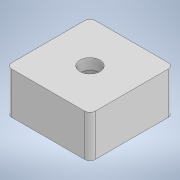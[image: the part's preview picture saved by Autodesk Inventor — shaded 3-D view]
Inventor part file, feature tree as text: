
AUTODESK INVENTOR PART (.ipt)
format: ipt  version: 2021 (Build 250183000, 183)  size: 146,432 bytes
history: native  units: mm
features: sketch x5, extrude x3, other x2, hole x2, fillet x1, projected_geometry x1
ambient origin geometry x8: Origin, YZ Plane, XZ Plane, XY Plane, X Axis, Y Axis, Z Axis, Center Point
bodies: Body1 (feature_tree)
feature tree (14):
  other  "實體1"
  extrude  "擠出2"  Depth=144.0mm TaperAngle=0.0deg
  extrude  "擠出3"  Depth=20.0mm
  hole  "孔1"  [1 undecoded]
  hole  "孔2"  [1 undecoded]
  fillet  "圓角1"  Radius=30.0mm
  extrude  "擠出1"  Depth=20.2mm
  sketch  "草圖1"
  sketch  "草圖2"
  other  "實體2"
  sketch  "草圖3"
  projected_geometry  "投影迴路1"
  sketch  "草圖4"
  sketch  "草圖5"
note: 2 required parameter values undecoded (feature->parameter linkage not recoverable at this tier; creation-order binding heuristic only, values carry confidence <= 0.55)
